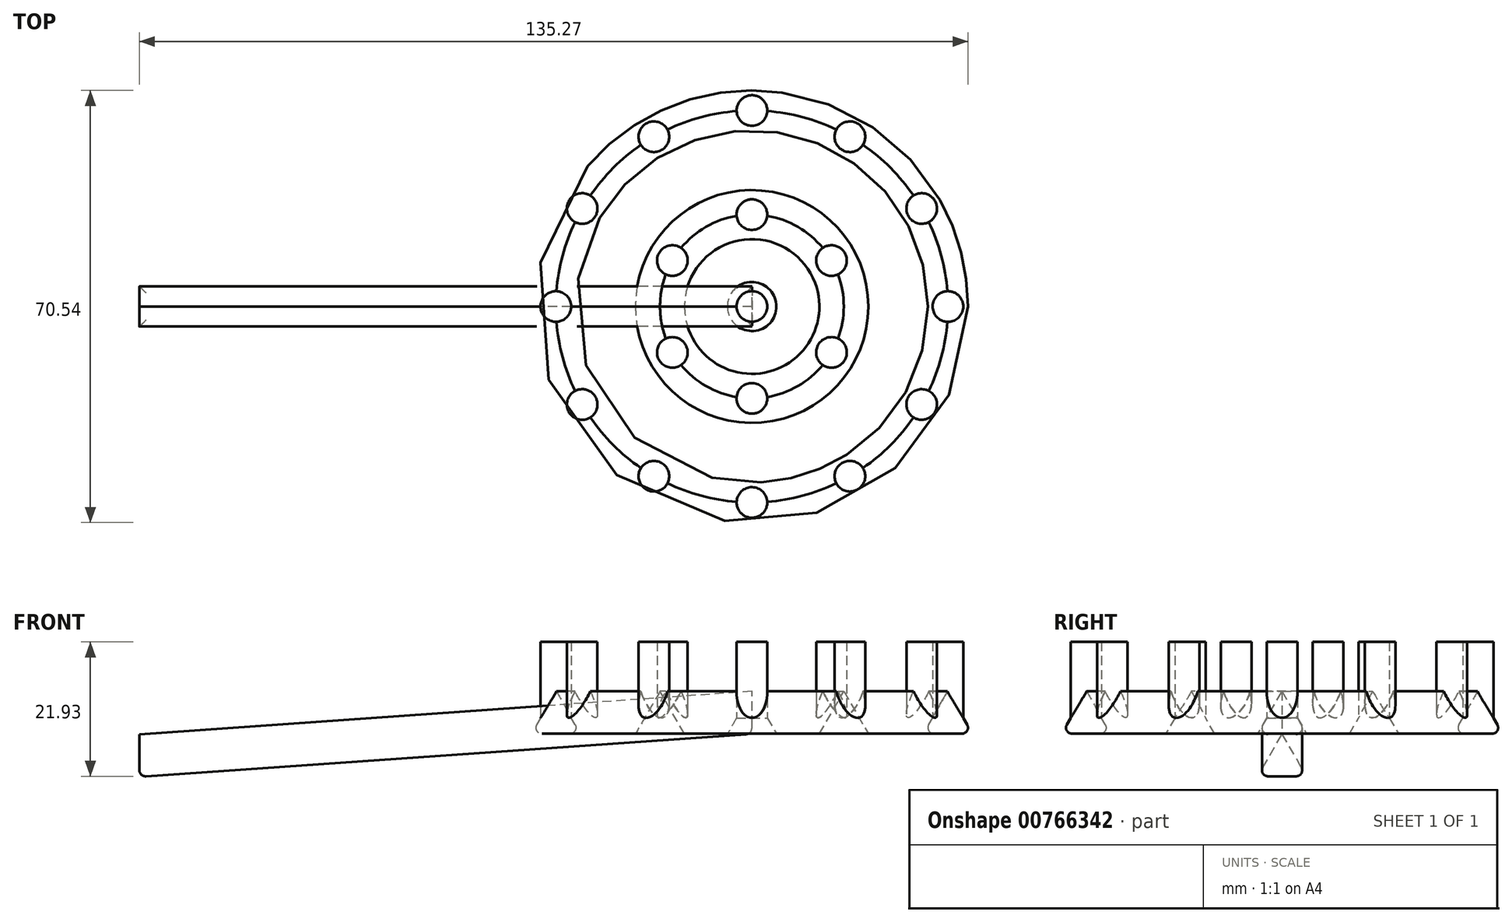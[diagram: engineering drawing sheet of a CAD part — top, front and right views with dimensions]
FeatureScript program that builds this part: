
annotation { "Feature Type Name" : "Feature", "Feature Type Description" : "" }
export const myFeature = defineFeature(function(context is Context, id is Id, definition is map)
    precondition{}
    {
        {
            var Q0;
            Q0=qCreatedBy(makeId("Top.planeOp"),FACE);
            var sketch = newSketch(context, id + "F0", { "sketchPlane" : qUnion([Q0])});
            skCircle(sketch, "E0", {"center": v(0, 0) * mm, "radius": 2.5 * mm});
            skCircle(sketch, "E1.1.0", {"center": v(16, 4.29) * mm, "radius": 2.5 * mm});
            skCircle(sketch, "E1.2.0", {"center": v(27.71, 16) * mm, "radius": 2.5 * mm});
            skPoint(sketch, "E1.center", {"position": v(0, 32) * mm});
            skCircle(sketch, "E2.1.3.0", {"center": v(32, 32) * mm, "radius": 2.5 * mm});
            skCircle(sketch, "E2.1.4.0", {"center": v(27.71, 48) * mm, "radius": 2.5 * mm});
            skCircle(sketch, "E2.1.5.0", {"center": v(16, 59.71) * mm, "radius": 2.5 * mm});
            skCircle(sketch, "E2.1.6.0", {"center": v(0, 64) * mm, "radius": 2.5 * mm});
            skCircle(sketch, "E2.1.7.0", {"center": v(-16, 59.71) * mm, "radius": 2.5 * mm});
            skCircle(sketch, "E2.1.8.0", {"center": v(-27.71, 48) * mm, "radius": 2.5 * mm});
            skCircle(sketch, "E2.1.9.0", {"center": v(-32, 32) * mm, "radius": 2.5 * mm});
            skCircle(sketch, "E2.1.10.0", {"center": v(-27.71, 16) * mm, "radius": 2.5 * mm});
            skCircle(sketch, "E2.1.11.0", {"center": v(-16, 4.29) * mm, "radius": 2.5 * mm});
            skLineSegment(sketch, "E3", {"start": v(0, 32) * mm, "end": v(0, 17) * mm, "construction": true});
            skCircle(sketch, "E4", {"center": v(0, 17) * mm, "radius": 2.5 * mm});
            skCircle(sketch, "E5", {"center": v(0, 32) * mm, "radius": 2.5 * mm});
            skCircle(sketch, "E6.1.0", {"center": v(13, 24.5) * mm, "radius": 2.5 * mm});
            skCircle(sketch, "E6.2.0", {"center": v(13, 39.5) * mm, "radius": 2.5 * mm});
            skCircle(sketch, "E6.3.0", {"center": v(0, 47) * mm, "radius": 2.5 * mm});
            skCircle(sketch, "E6.4.0", {"center": v(-13, 39.5) * mm, "radius": 2.5 * mm});
            skCircle(sketch, "E6.5.0", {"center": v(-13, 24.5) * mm, "radius": 2.5 * mm});
            skCircle(sketch, "E7", {"center": v(0, 32) * mm, "radius": 15 * mm});
            skCircle(sketch, "E8", {"center": v(0, 32) * mm, "radius": 32 * mm});
            skSolve(sketch);
        }
        {
            var Q0;
            Q0=qCreatedBy(makeId("Right.planeOp"),FACE);
            var sketch = newSketch(context, id + "F1", { "sketchPlane" : qUnion([Q0])});
            skLineSegment(sketch, "E9", {"start": v(-4, 0) * mm, "end": v(4, 0) * mm});
            skLineSegment(sketch, "E10", {"start": v(4, 0) * mm, "end": v(0, 6.93) * mm});
            skLineSegment(sketch, "E11", {"start": v(0, 6.93) * mm, "end": v(-4, 0) * mm});
            skLineSegment(sketch, "E12.direction1", {"start": v(-4, 0) * mm, "end": v(21, 0) * mm, "construction": true});
            skLineSegment(sketch, "E13.1.0.0", {"start": v(13, 0) * mm, "end": v(38, 0) * mm, "construction": true});
            skLineSegment(sketch, "E13.1.0.1", {"start": v(17, 6.93) * mm, "end": v(13, 0) * mm});
            skLineSegment(sketch, "E13.1.0.2", {"start": v(21, 0) * mm, "end": v(17, 6.93) * mm});
            skLineSegment(sketch, "E13.direction1", {"start": v(-4, 0) * mm, "end": v(13, 0) * mm, "construction": true});
            skLineSegment(sketch, "E14", {"start": v(21, 0) * mm, "end": v(32, 0) * mm});
            skLineSegment(sketch, "E15", {"start": v(21, 0) * mm, "end": v(13, 0) * mm});
            skLineSegment(sketch, "E16", {"start": v(32, 0) * mm, "end": v(32, 10.68) * mm});
            skLineSegment(sketch, "E17", {"start": v(13, 0) * mm, "end": v(17, 0) * mm});
            skLineSegment(sketch, "E18", {"start": v(17, 0) * mm, "end": v(21, 0) * mm});
            skLineSegment(sketch, "E19", {"start": v(28, 0) * mm, "end": v(32, 6.93) * mm});
            skLineSegment(sketch, "E20", {"start": v(32, 6.93) * mm, "end": v(36, 0) * mm});
            skLineSegment(sketch, "E21", {"start": v(36, 0) * mm, "end": v(28, 0) * mm});
            skSolve(sketch);
        }
        {
            var Q0;
            Q0=makeQuery(id+"F1.imprint","IMPRINT",FACE,{"disambiguationData":[TD([[makeQuery(id+"F1.imprint","IMPRINT",EDGE,{"derivedFrom":sQuery(id+"F1.wireOp",EDGE,"E13.1.0.1")}),1.0]])]});
            var Q1;
            Q1=makeQuery(id+"F1.imprint","IMPRINT",FACE,{"disambiguationData":[TD([[makeQuery(id+"F1.imprint","IMPRINT",EDGE,{"derivedFrom":sQuery(id+"F1.wireOp",EDGE,"E9")}),1.0]])]});
            var Q2;
            {var subQ0=sQuery(id+"F1.wireOp",EDGE,"E12.1.0.0");Q2=makeQuery(id+"F1.imprint","IMPRINT",FACE,{"disambiguationData":[TD([[makeQuery(id+"F1.imprint","IMPRINT",EDGE,{"derivedFrom":subQ0}),1.0]])]});}
            var Q3;
            {var subQ3=sQuery(id+"F1.wireOp",EDGE,"E19");Q3=makeQuery(id+"F1.imprint","IMPRINT",FACE,{"disambiguationData":[TD([[makeQuery(id+"F1.imprint","IMPRINT",EDGE,{"derivedFrom":subQ3}),-1.0]])]});}
            var Q4;
            Q4=sQuery(id+"F1.wireOp",EDGE,"E16");
            revolve(context, id + "F2", {"surfaceOperationType" : NewSurfaceOperationType.NEW, "entities" : qUnion([Q0, Q1, Q2, Q3]), "axis" : qUnion([Q4]), "revolveType" : RevolveType.FULL});
        }
        {
            var Q0;
            {var subQ0=sQuery(id+"F0.wireOp",EDGE,"E8");var subQ1=sQuery(id+"F0.wireOp",EDGE,"E2.1.11.0");var subQ2=makeQuery(id+"F0.imprint","INTERSECT",VERTEX,{"disambiguationData":[OD(0.0)],"derivedFrom":[subQ1,subQ0]});Q0=makeQuery(id+"F0.imprint","IMPRINT",FACE,{"disambiguationData":[TD([[makeQuery(id+"F0.imprint","IMPRINT",EDGE,{"disambiguationData":[TD([[subQ2,-1.0]])],"derivedFrom":subQ1}),1.0]])]});}
            var Q1;
            {var subQ0=sQuery(id+"F0.wireOp",EDGE,"E8");var subQ1=sQuery(id+"F0.wireOp",EDGE,"E2.1.11.0");var subQ2=makeQuery(id+"F0.imprint","INTERSECT",VERTEX,{"disambiguationData":[OD(0.0)],"derivedFrom":[subQ1,subQ0]});Q1=makeQuery(id+"F0.imprint","IMPRINT",FACE,{"disambiguationData":[TD([[makeQuery(id+"F0.imprint","IMPRINT",EDGE,{"disambiguationData":[TD([[subQ2,1.0]])],"derivedFrom":subQ1}),1.0]])]});}
            var Q2;
            {var subQ0=sQuery(id+"F0.wireOp",EDGE,"E8");var subQ1=sQuery(id+"F0.wireOp",EDGE,"E2.1.10.0");var subQ2=makeQuery(id+"F0.imprint","INTERSECT",VERTEX,{"disambiguationData":[OD(0.0)],"derivedFrom":[subQ1,subQ0]});Q2=makeQuery(id+"F0.imprint","IMPRINT",FACE,{"disambiguationData":[TD([[makeQuery(id+"F0.imprint","IMPRINT",EDGE,{"disambiguationData":[TD([[subQ2,-1.0]])],"derivedFrom":subQ1}),1.0]])]});}
            var Q3;
            {var subQ0=sQuery(id+"F0.wireOp",EDGE,"E8");var subQ1=sQuery(id+"F0.wireOp",EDGE,"E2.1.10.0");var subQ2=makeQuery(id+"F0.imprint","INTERSECT",VERTEX,{"disambiguationData":[OD(0.0)],"derivedFrom":[subQ1,subQ0]});Q3=makeQuery(id+"F0.imprint","IMPRINT",FACE,{"disambiguationData":[TD([[makeQuery(id+"F0.imprint","IMPRINT",EDGE,{"disambiguationData":[TD([[subQ2,1.0]])],"derivedFrom":subQ1}),1.0]])]});}
            var Q4;
            {var subQ0=sQuery(id+"F0.wireOp",EDGE,"E8");var subQ1=sQuery(id+"F0.wireOp",EDGE,"E2.1.9.0");var subQ2=makeQuery(id+"F0.imprint","INTERSECT",VERTEX,{"disambiguationData":[OD(0.0)],"derivedFrom":[subQ1,subQ0]});Q4=makeQuery(id+"F0.imprint","IMPRINT",FACE,{"disambiguationData":[TD([[makeQuery(id+"F0.imprint","IMPRINT",EDGE,{"disambiguationData":[TD([[subQ2,-1.0]])],"derivedFrom":subQ1}),1.0]])]});}
            var Q5;
            {var subQ0=sQuery(id+"F0.wireOp",EDGE,"E8");var subQ1=sQuery(id+"F0.wireOp",EDGE,"E2.1.9.0");var subQ2=makeQuery(id+"F0.imprint","INTERSECT",VERTEX,{"disambiguationData":[OD(0.0)],"derivedFrom":[subQ1,subQ0]});Q5=makeQuery(id+"F0.imprint","IMPRINT",FACE,{"disambiguationData":[TD([[makeQuery(id+"F0.imprint","IMPRINT",EDGE,{"disambiguationData":[TD([[subQ2,1.0]])],"derivedFrom":subQ1}),1.0]])]});}
            var Q6;
            {var subQ0=sQuery(id+"F0.wireOp",EDGE,"E8");var subQ1=sQuery(id+"F0.wireOp",EDGE,"E2.1.8.0");var subQ2=makeQuery(id+"F0.imprint","INTERSECT",VERTEX,{"disambiguationData":[OD(0.0)],"derivedFrom":[subQ1,subQ0]});Q6=makeQuery(id+"F0.imprint","IMPRINT",FACE,{"disambiguationData":[TD([[makeQuery(id+"F0.imprint","IMPRINT",EDGE,{"disambiguationData":[TD([[subQ2,1.0]])],"derivedFrom":subQ1}),1.0]])]});}
            var Q7;
            {var subQ0=sQuery(id+"F0.wireOp",EDGE,"E8");var subQ1=sQuery(id+"F0.wireOp",EDGE,"E2.1.8.0");var subQ2=makeQuery(id+"F0.imprint","INTERSECT",VERTEX,{"disambiguationData":[OD(0.0)],"derivedFrom":[subQ1,subQ0]});Q7=makeQuery(id+"F0.imprint","IMPRINT",FACE,{"disambiguationData":[TD([[makeQuery(id+"F0.imprint","IMPRINT",EDGE,{"disambiguationData":[TD([[subQ2,-1.0]])],"derivedFrom":subQ1}),1.0]])]});}
            var Q8;
            {var subQ0=sQuery(id+"F0.wireOp",EDGE,"E8");var subQ1=sQuery(id+"F0.wireOp",EDGE,"E2.1.7.0");var subQ2=makeQuery(id+"F0.imprint","INTERSECT",VERTEX,{"disambiguationData":[OD(0.0)],"derivedFrom":[subQ1,subQ0]});Q8=makeQuery(id+"F0.imprint","IMPRINT",FACE,{"disambiguationData":[TD([[makeQuery(id+"F0.imprint","IMPRINT",EDGE,{"disambiguationData":[TD([[subQ2,-1.0]])],"derivedFrom":subQ1}),1.0]])]});}
            var Q9;
            {var subQ0=sQuery(id+"F0.wireOp",EDGE,"E8");var subQ1=sQuery(id+"F0.wireOp",EDGE,"E2.1.7.0");var subQ2=makeQuery(id+"F0.imprint","INTERSECT",VERTEX,{"disambiguationData":[OD(0.0)],"derivedFrom":[subQ1,subQ0]});Q9=makeQuery(id+"F0.imprint","IMPRINT",FACE,{"disambiguationData":[TD([[makeQuery(id+"F0.imprint","IMPRINT",EDGE,{"disambiguationData":[TD([[subQ2,1.0]])],"derivedFrom":subQ1}),1.0]])]});}
            var Q10;
            {var subQ0=sQuery(id+"F0.wireOp",EDGE,"E8");var subQ1=sQuery(id+"F0.wireOp",EDGE,"E2.1.6.0");var subQ2=makeQuery(id+"F0.imprint","INTERSECT",VERTEX,{"disambiguationData":[OD(0.0)],"derivedFrom":[subQ1,subQ0]});Q10=makeQuery(id+"F0.imprint","IMPRINT",FACE,{"disambiguationData":[TD([[makeQuery(id+"F0.imprint","IMPRINT",EDGE,{"disambiguationData":[TD([[subQ2,-1.0]])],"derivedFrom":subQ1}),1.0]])]});}
            var Q11;
            {var subQ0=sQuery(id+"F0.wireOp",EDGE,"E8");var subQ1=sQuery(id+"F0.wireOp",EDGE,"E2.1.5.0");var subQ2=makeQuery(id+"F0.imprint","INTERSECT",VERTEX,{"disambiguationData":[OD(0.0)],"derivedFrom":[subQ1,subQ0]});Q11=makeQuery(id+"F0.imprint","IMPRINT",FACE,{"disambiguationData":[TD([[makeQuery(id+"F0.imprint","IMPRINT",EDGE,{"disambiguationData":[TD([[subQ2,-1.0]])],"derivedFrom":subQ1}),1.0]])]});}
            var Q12;
            {var subQ0=sQuery(id+"F0.wireOp",EDGE,"E8");var subQ1=sQuery(id+"F0.wireOp",EDGE,"E2.1.4.0");var subQ2=makeQuery(id+"F0.imprint","INTERSECT",VERTEX,{"disambiguationData":[OD(0.0)],"derivedFrom":[subQ1,subQ0]});Q12=makeQuery(id+"F0.imprint","IMPRINT",FACE,{"disambiguationData":[TD([[makeQuery(id+"F0.imprint","IMPRINT",EDGE,{"disambiguationData":[TD([[subQ2,1.0]])],"derivedFrom":subQ1}),1.0]])]});}
            var Q13;
            {var subQ0=sQuery(id+"F0.wireOp",EDGE,"E8");var subQ1=sQuery(id+"F0.wireOp",EDGE,"E0");var subQ2=makeQuery(id+"F0.imprint","INTERSECT",VERTEX,{"disambiguationData":[OD(0.0)],"derivedFrom":[subQ1,subQ0]});Q13=makeQuery(id+"F0.imprint","IMPRINT",FACE,{"disambiguationData":[TD([[makeQuery(id+"F0.imprint","IMPRINT",EDGE,{"disambiguationData":[TD([[subQ2,1.0]])],"derivedFrom":subQ1}),1.0]])]});}
            var Q14;
            {var subQ0=sQuery(id+"F0.wireOp",EDGE,"E8");var subQ1=sQuery(id+"F0.wireOp",EDGE,"E1.1.0");var subQ2=makeQuery(id+"F0.imprint","INTERSECT",VERTEX,{"disambiguationData":[OD(0.0)],"derivedFrom":[subQ1,subQ0]});Q14=makeQuery(id+"F0.imprint","IMPRINT",FACE,{"disambiguationData":[TD([[makeQuery(id+"F0.imprint","IMPRINT",EDGE,{"disambiguationData":[TD([[subQ2,-1.0]])],"derivedFrom":subQ1}),1.0]])]});}
            var Q15;
            {var subQ0=sQuery(id+"F0.wireOp",EDGE,"E8");var subQ1=sQuery(id+"F0.wireOp",EDGE,"E1.1.0");var subQ2=makeQuery(id+"F0.imprint","INTERSECT",VERTEX,{"disambiguationData":[OD(0.0)],"derivedFrom":[subQ1,subQ0]});Q15=makeQuery(id+"F0.imprint","IMPRINT",FACE,{"disambiguationData":[TD([[makeQuery(id+"F0.imprint","IMPRINT",EDGE,{"disambiguationData":[TD([[subQ2,1.0]])],"derivedFrom":subQ1}),1.0]])]});}
            var Q16;
            {var subQ0=sQuery(id+"F0.wireOp",EDGE,"E8");var subQ1=sQuery(id+"F0.wireOp",EDGE,"E1.2.0");var subQ2=makeQuery(id+"F0.imprint","INTERSECT",VERTEX,{"disambiguationData":[OD(0.0)],"derivedFrom":[subQ1,subQ0]});Q16=makeQuery(id+"F0.imprint","IMPRINT",FACE,{"disambiguationData":[TD([[makeQuery(id+"F0.imprint","IMPRINT",EDGE,{"disambiguationData":[TD([[subQ2,-1.0]])],"derivedFrom":subQ1}),1.0]])]});}
            var Q17;
            {var subQ0=sQuery(id+"F0.wireOp",EDGE,"E8");var subQ1=sQuery(id+"F0.wireOp",EDGE,"E1.2.0");var subQ2=makeQuery(id+"F0.imprint","INTERSECT",VERTEX,{"disambiguationData":[OD(0.0)],"derivedFrom":[subQ1,subQ0]});Q17=makeQuery(id+"F0.imprint","IMPRINT",FACE,{"disambiguationData":[TD([[makeQuery(id+"F0.imprint","IMPRINT",EDGE,{"disambiguationData":[TD([[subQ2,1.0]])],"derivedFrom":subQ1}),1.0]])]});}
            var Q18;
            {var subQ0=sQuery(id+"F0.wireOp",EDGE,"E8");var subQ1=sQuery(id+"F0.wireOp",EDGE,"E2.1.3.0");var subQ2=makeQuery(id+"F0.imprint","INTERSECT",VERTEX,{"disambiguationData":[OD(0.0)],"derivedFrom":[subQ1,subQ0]});Q18=makeQuery(id+"F0.imprint","IMPRINT",FACE,{"disambiguationData":[TD([[makeQuery(id+"F0.imprint","IMPRINT",EDGE,{"disambiguationData":[TD([[subQ2,1.0]])],"derivedFrom":subQ1}),1.0]])]});}
            var Q19;
            {var subQ0=sQuery(id+"F0.wireOp",EDGE,"E8");var subQ1=sQuery(id+"F0.wireOp",EDGE,"E2.1.3.0");var subQ2=makeQuery(id+"F0.imprint","INTERSECT",VERTEX,{"disambiguationData":[OD(0.0)],"derivedFrom":[subQ1,subQ0]});Q19=makeQuery(id+"F0.imprint","IMPRINT",FACE,{"disambiguationData":[TD([[makeQuery(id+"F0.imprint","IMPRINT",EDGE,{"disambiguationData":[TD([[subQ2,-1.0]])],"derivedFrom":subQ1}),1.0]])]});}
            var Q20;
            {var subQ0=sQuery(id+"F0.wireOp",EDGE,"E7");var subQ1=sQuery(id+"F0.wireOp",EDGE,"E6.1.0");var subQ2=makeQuery(id+"F0.imprint","INTERSECT",VERTEX,{"disambiguationData":[OD(0.0)],"derivedFrom":[subQ1,subQ0]});Q20=makeQuery(id+"F0.imprint","IMPRINT",FACE,{"disambiguationData":[TD([[makeQuery(id+"F0.imprint","IMPRINT",EDGE,{"disambiguationData":[TD([[subQ2,-1.0]])],"derivedFrom":subQ1}),1.0]])]});}
            var Q21;
            {var subQ0=sQuery(id+"F0.wireOp",EDGE,"E7");var subQ1=sQuery(id+"F0.wireOp",EDGE,"E6.1.0");var subQ2=makeQuery(id+"F0.imprint","INTERSECT",VERTEX,{"disambiguationData":[OD(0.0)],"derivedFrom":[subQ1,subQ0]});Q21=makeQuery(id+"F0.imprint","IMPRINT",FACE,{"disambiguationData":[TD([[makeQuery(id+"F0.imprint","IMPRINT",EDGE,{"disambiguationData":[TD([[subQ2,1.0]])],"derivedFrom":subQ1}),1.0]])]});}
            var Q22;
            {var subQ0=sQuery(id+"F0.wireOp",EDGE,"E7");var subQ1=sQuery(id+"F0.wireOp",EDGE,"E6.2.0");var subQ2=makeQuery(id+"F0.imprint","INTERSECT",VERTEX,{"disambiguationData":[OD(0.0)],"derivedFrom":[subQ1,subQ0]});Q22=makeQuery(id+"F0.imprint","IMPRINT",FACE,{"disambiguationData":[TD([[makeQuery(id+"F0.imprint","IMPRINT",EDGE,{"disambiguationData":[TD([[subQ2,1.0]])],"derivedFrom":subQ1}),1.0]])]});}
            var Q23;
            {var subQ0=sQuery(id+"F0.wireOp",EDGE,"E7");var subQ1=sQuery(id+"F0.wireOp",EDGE,"E6.3.0");var subQ2=makeQuery(id+"F0.imprint","INTERSECT",VERTEX,{"disambiguationData":[OD(0.0)],"derivedFrom":[subQ1,subQ0]});Q23=makeQuery(id+"F0.imprint","IMPRINT",FACE,{"disambiguationData":[TD([[makeQuery(id+"F0.imprint","IMPRINT",EDGE,{"disambiguationData":[TD([[subQ2,1.0]])],"derivedFrom":subQ1}),1.0]])]});}
            var Q24;
            {var subQ0=sQuery(id+"F0.wireOp",EDGE,"E7");var subQ1=sQuery(id+"F0.wireOp",EDGE,"E6.3.0");var subQ2=makeQuery(id+"F0.imprint","INTERSECT",VERTEX,{"disambiguationData":[OD(0.0)],"derivedFrom":[subQ1,subQ0]});Q24=makeQuery(id+"F0.imprint","IMPRINT",FACE,{"disambiguationData":[TD([[makeQuery(id+"F0.imprint","IMPRINT",EDGE,{"disambiguationData":[TD([[subQ2,-1.0]])],"derivedFrom":subQ1}),1.0]])]});}
            var Q25;
            Q25=makeQuery(id+"F0.imprint","IMPRINT",FACE,{"disambiguationData":[TD([[makeQuery(id+"F0.imprint","IMPRINT",EDGE,{"derivedFrom":sQuery(id+"F0.wireOp",EDGE,"E5")}),1.0]])]});
            var Q26;
            {var subQ0=sQuery(id+"F0.wireOp",EDGE,"E7");var subQ1=sQuery(id+"F0.wireOp",EDGE,"E6.2.0");var subQ2=makeQuery(id+"F0.imprint","INTERSECT",VERTEX,{"disambiguationData":[OD(0.0)],"derivedFrom":[subQ1,subQ0]});Q26=makeQuery(id+"F0.imprint","IMPRINT",FACE,{"disambiguationData":[TD([[makeQuery(id+"F0.imprint","IMPRINT",EDGE,{"disambiguationData":[TD([[subQ2,-1.0]])],"derivedFrom":subQ1}),1.0]])]});}
            var Q27;
            {var subQ0=sQuery(id+"F0.wireOp",EDGE,"E7");var subQ1=sQuery(id+"F0.wireOp",EDGE,"E4");var subQ2=makeQuery(id+"F0.imprint","INTERSECT",VERTEX,{"disambiguationData":[OD(0.0)],"derivedFrom":[subQ1,subQ0]});Q27=makeQuery(id+"F0.imprint","IMPRINT",FACE,{"disambiguationData":[TD([[makeQuery(id+"F0.imprint","IMPRINT",EDGE,{"disambiguationData":[TD([[subQ2,-1.0]])],"derivedFrom":subQ1}),1.0]])]});}
            var Q28;
            {var subQ0=sQuery(id+"F0.wireOp",EDGE,"E7");var subQ1=sQuery(id+"F0.wireOp",EDGE,"E6.5.0");var subQ2=makeQuery(id+"F0.imprint","INTERSECT",VERTEX,{"disambiguationData":[OD(0.0)],"derivedFrom":[subQ1,subQ0]});Q28=makeQuery(id+"F0.imprint","IMPRINT",FACE,{"disambiguationData":[TD([[makeQuery(id+"F0.imprint","IMPRINT",EDGE,{"disambiguationData":[TD([[subQ2,-1.0]])],"derivedFrom":subQ1}),1.0]])]});}
            var Q29;
            {var subQ0=sQuery(id+"F0.wireOp",EDGE,"E7");var subQ1=sQuery(id+"F0.wireOp",EDGE,"E6.5.0");var subQ2=makeQuery(id+"F0.imprint","INTERSECT",VERTEX,{"disambiguationData":[OD(0.0)],"derivedFrom":[subQ1,subQ0]});Q29=makeQuery(id+"F0.imprint","IMPRINT",FACE,{"disambiguationData":[TD([[makeQuery(id+"F0.imprint","IMPRINT",EDGE,{"disambiguationData":[TD([[subQ2,1.0]])],"derivedFrom":subQ1}),1.0]])]});}
            var Q30;
            {var subQ0=sQuery(id+"F0.wireOp",EDGE,"E7");var subQ1=sQuery(id+"F0.wireOp",EDGE,"E4");var subQ2=makeQuery(id+"F0.imprint","INTERSECT",VERTEX,{"disambiguationData":[OD(0.0)],"derivedFrom":[subQ1,subQ0]});Q30=makeQuery(id+"F0.imprint","IMPRINT",FACE,{"disambiguationData":[TD([[makeQuery(id+"F0.imprint","IMPRINT",EDGE,{"disambiguationData":[TD([[subQ2,1.0]])],"derivedFrom":subQ1}),1.0]])]});}
            var Q31;
            {var subQ0=sQuery(id+"F0.wireOp",EDGE,"E7");var subQ1=sQuery(id+"F0.wireOp",EDGE,"E6.4.0");var subQ2=makeQuery(id+"F0.imprint","INTERSECT",VERTEX,{"disambiguationData":[OD(0.0)],"derivedFrom":[subQ1,subQ0]});Q31=makeQuery(id+"F0.imprint","IMPRINT",FACE,{"disambiguationData":[TD([[makeQuery(id+"F0.imprint","IMPRINT",EDGE,{"disambiguationData":[TD([[subQ2,1.0]])],"derivedFrom":subQ1}),1.0]])]});}
            var Q32;
            {var subQ0=sQuery(id+"F0.wireOp",EDGE,"E7");var subQ1=sQuery(id+"F0.wireOp",EDGE,"E6.4.0");var subQ2=makeQuery(id+"F0.imprint","INTERSECT",VERTEX,{"disambiguationData":[OD(0.0)],"derivedFrom":[subQ1,subQ0]});Q32=makeQuery(id+"F0.imprint","IMPRINT",FACE,{"disambiguationData":[TD([[makeQuery(id+"F0.imprint","IMPRINT",EDGE,{"disambiguationData":[TD([[subQ2,-1.0]])],"derivedFrom":subQ1}),1.0]])]});}
            var Q33;
            {var subQ0=sQuery(id+"F0.wireOp",EDGE,"E8");var subQ1=sQuery(id+"F0.wireOp",EDGE,"E0");var subQ2=makeQuery(id+"F0.imprint","INTERSECT",VERTEX,{"disambiguationData":[OD(0.0)],"derivedFrom":[subQ1,subQ0]});Q33=makeQuery(id+"F0.imprint","IMPRINT",FACE,{"disambiguationData":[TD([[makeQuery(id+"F0.imprint","IMPRINT",EDGE,{"disambiguationData":[TD([[subQ2,-1.0]])],"derivedFrom":subQ1}),1.0]])]});}
            var Q34;
            {var subQ0=sQuery(id+"F0.wireOp",EDGE,"E8");var subQ1=sQuery(id+"F0.wireOp",EDGE,"E2.1.6.0");var subQ2=makeQuery(id+"F0.imprint","INTERSECT",VERTEX,{"disambiguationData":[OD(0.0)],"derivedFrom":[subQ1,subQ0]});Q34=makeQuery(id+"F0.imprint","IMPRINT",FACE,{"disambiguationData":[TD([[makeQuery(id+"F0.imprint","IMPRINT",EDGE,{"disambiguationData":[TD([[subQ2,1.0]])],"derivedFrom":subQ1}),1.0]])]});}
            var Q35;
            {var subQ0=sQuery(id+"F0.wireOp",EDGE,"E8");var subQ1=sQuery(id+"F0.wireOp",EDGE,"E2.1.4.0");var subQ2=makeQuery(id+"F0.imprint","INTERSECT",VERTEX,{"disambiguationData":[OD(0.0)],"derivedFrom":[subQ1,subQ0]});Q35=makeQuery(id+"F0.imprint","IMPRINT",FACE,{"disambiguationData":[TD([[makeQuery(id+"F0.imprint","IMPRINT",EDGE,{"disambiguationData":[TD([[subQ2,-1.0]])],"derivedFrom":subQ1}),1.0]])]});}
            var Q36;
            {var subQ0=sQuery(id+"F0.wireOp",EDGE,"E8");var subQ1=sQuery(id+"F0.wireOp",EDGE,"E2.1.5.0");var subQ2=makeQuery(id+"F0.imprint","INTERSECT",VERTEX,{"disambiguationData":[OD(0.0)],"derivedFrom":[subQ1,subQ0]});Q36=makeQuery(id+"F0.imprint","IMPRINT",FACE,{"disambiguationData":[TD([[makeQuery(id+"F0.imprint","IMPRINT",EDGE,{"disambiguationData":[TD([[subQ2,1.0]])],"derivedFrom":subQ1}),1.0]])]});}
            extrude(context, id + "F3", {"entities" : qUnion([Q0, Q1, Q2, Q3, Q4, Q5, Q6, Q7, Q8, Q9, Q10, Q11, Q12, Q13, Q14, Q15, Q16, Q17, Q18, Q19, Q20, Q21, Q22, Q23, Q24, Q25, Q26, Q27, Q28, Q29, Q30, Q31, Q32, Q33, Q34, Q35, Q36]), "operationType" : NewBodyOperationType.ADD, "depth" : 15 * mm, "offsetDistance" : 25 * mm});
        }
        {
            var Q0;
            Q0=qCreatedBy(makeId("Front.planeOp"),FACE);
            var sketch = newSketch(context, id + "F4", { "sketchPlane" : qUnion([Q0])});
            skLineSegment(sketch, "E22", {"start": v(0, 0) * mm, "end": v(-100, -7) * mm});
            skSolve(sketch);
        }
        {
            var Q0;
            {var subQ3=sQuery(id+"F1.wireOp",EDGE,"E20");Q0=makeQuery(id+"F1.imprint","IMPRINT",FACE,{"disambiguationData":[TD([[makeQuery(id+"F1.imprint","IMPRINT",EDGE,{"derivedFrom":subQ3}),-1.0]])]});}
            var Q1;
            {var subQ3=sQuery(id+"F1.wireOp",EDGE,"E19");Q1=makeQuery(id+"F1.imprint","IMPRINT",FACE,{"disambiguationData":[TD([[makeQuery(id+"F1.imprint","IMPRINT",EDGE,{"derivedFrom":subQ3}),-1.0]])]});}
            var Q2;
            Q2=sQuery(id+"F4.wireOp",EDGE,"E22");
            sweep(context, id + "F5", {"profiles" : qUnion([Q0, Q1]), "path" : qUnion([Q2])});
        }
        {
            var Q0;
            Q0=makeQuery(id+"F5.opSweep","SWEPT_FACE",FACE,{"disambiguationData":[OSD([sQuery(id+"F1.wireOp",EDGE,"E21"),sQuery(id+"F4.wireOp",EDGE,"E22")])]});
            var Q1;
            Q1=makeQuery(id+"F2.opRevolve","SWEPT_FACE",FACE,{"disambiguationData":[OSD([sQuery(id+"F1.wireOp",EDGE,"E9")])]});
            var Q2;
            Q2=makeQuery(id+"F2.opRevolve","SWEPT_FACE",FACE,{"disambiguationData":[OSD([sQuery(id+"F1.wireOp",EDGE,"E17"),sQuery(id+"F1.wireOp",EDGE,"E18")])]});
            var Q3;
            Q3=makeQuery(id+"F2.opRevolve","SWEPT_FACE",FACE,{"disambiguationData":[OSD([sQuery(id+"F1.wireOp",EDGE,"E21")])]});
            fillet(context, id + "F6", {"entities" : qUnion([Q0, Q1, Q2, Q3]), "radius" : 1 * mm, "tangentPropagation" : true, "allowEdgeOverflow" : false});
        }
    });
